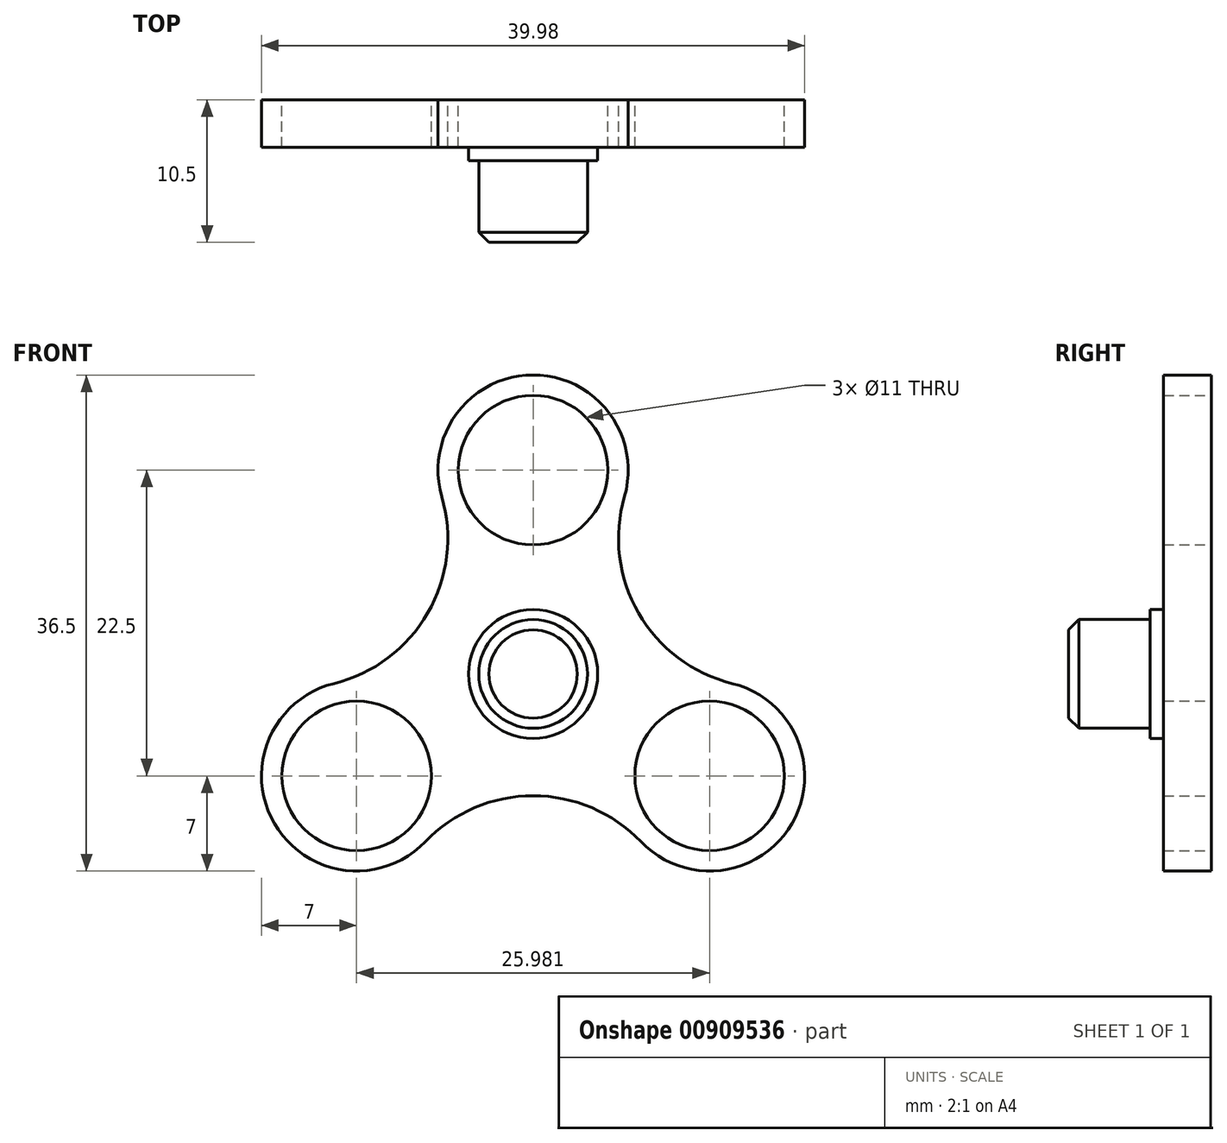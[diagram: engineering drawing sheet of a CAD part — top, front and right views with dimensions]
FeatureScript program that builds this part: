
annotation { "Feature Type Name" : "Feature", "Feature Type Description" : "" }
export const myFeature = defineFeature(function(context is Context, id is Id, definition is map)
    precondition{}
    {
        {
            var Q0;
            Q0=qCreatedBy(makeId("Front.planeOp"),FACE);
            var sketch = newSketch(context, id + "F0", { "sketchPlane" : qUnion([Q0])});
            skCircle(sketch, "E0", {"center": v(0, 0) * mm, "radius": 11 * mm});
            skCircle(sketch, "E1.cCircle", {"center": v(0, 0) * mm, "radius": 30 * mm, "construction": true});
            skLineSegment(sketch, "E1.0", {"start": v(0, 30) * mm, "end": v(25.98, -15) * mm, "construction": true});
            skLineSegment(sketch, "E1.1", {"start": v(25.98, -15) * mm, "end": v(-25.98, -15) * mm, "construction": true});
            skLineSegment(sketch, "E1.2", {"start": v(-25.98, -15) * mm, "end": v(0, 30) * mm, "construction": true});
            skArc(sketch, "E2", {"start": v(10.56, 26.93) * mm, "mid": v(0, 41) * mm, "end": v(-10.56, 26.93) * mm});
            skArc(sketch, "E3", {"start": v(-28.6, -4.32) * mm, "mid": v(-35.5, -20.5) * mm, "end": v(-18.04, -22.61) * mm});
            skArc(sketch, "E4", {"start": v(18.04, -22.61) * mm, "mid": v(35.5, -20.5) * mm, "end": v(28.6, -4.32) * mm});
            skArc(sketch, "E5", {"start": v(-28.6, -4.32) * mm, "mid": v(-12.92, 7.46) * mm, "end": v(-10.56, 26.93) * mm});
            skArc(sketch, "E6", {"start": v(18.04, -22.61) * mm, "mid": v(0, -14.92) * mm, "end": v(-18.04, -22.61) * mm});
            skArc(sketch, "E7", {"start": v(10.56, 26.93) * mm, "mid": v(12.92, 7.46) * mm, "end": v(28.6, -4.32) * mm});
            skArc(sketch, "E8.0", {"start": v(13.44, 26.1) * mm, "mid": v(15.52, 8.96) * mm, "end": v(29.32, -1.4) * mm});
            skArc(sketch, "E8.1", {"start": v(-29.32, -1.4) * mm, "mid": v(-15.52, 8.96) * mm, "end": v(-13.44, 26.1) * mm});
            skArc(sketch, "E8.2", {"start": v(-29.32, -1.4) * mm, "mid": v(-38.1, -22) * mm, "end": v(-15.88, -24.7) * mm});
            skArc(sketch, "E8.3", {"start": v(13.44, 26.1) * mm, "mid": v(0, 44) * mm, "end": v(-13.44, 26.1) * mm});
            skArc(sketch, "E8.4", {"start": v(15.88, -24.7) * mm, "mid": v(0, -17.92) * mm, "end": v(-15.88, -24.7) * mm});
            skArc(sketch, "E8.5", {"start": v(15.88, -24.7) * mm, "mid": v(38.1, -22) * mm, "end": v(29.32, -1.4) * mm});
            skCircle(sketch, "E9", {"center": v(-25.98, -15) * mm, "radius": 11 * mm});
            skCircle(sketch, "E10", {"center": v(25.98, -15) * mm, "radius": 11 * mm});
            skCircle(sketch, "E11", {"center": v(0, 30) * mm, "radius": 11 * mm});
            skSolve(sketch);
        }
        {
            var Q0;
            Q0=makeQuery(id+"F0.imprint","IMPRINT",FACE,{"disambiguationData":[TD([[makeQuery(id+"F0.imprint","IMPRINT",EDGE,{"derivedFrom":sQuery(id+"F0.wireOp",EDGE,"E0")}),-1.0]])]});
            var Q1;
            {var subQ1=sQuery(id+"F0.wireOp",EDGE,"E5");Q1=makeQuery(id+"F0.imprint","IMPRINT",FACE,{"disambiguationData":[TD([[makeQuery(id+"F0.imprint","IMPRINT",EDGE,{"derivedFrom":subQ1}),1.0]])]});}
            extrude(context, id + "F1", {"entities" : qUnion([Q0, Q1]), "depth" : 7 * mm, "offsetDistance" : 25 * mm});
        }
        {
            var Q0;
            Q0=makeQuery(id+"F1.opExtrude","SWEPT_BODY",BODY,{"disambiguationData":[OSD([sQuery(id+"F0.wireOp",EDGE,"E0"),sQuery(id+"F0.wireOp",EDGE,"E8.0"),sQuery(id+"F0.wireOp",EDGE,"E8.1"),sQuery(id+"F0.wireOp",EDGE,"E8.2"),sQuery(id+"F0.wireOp",EDGE,"E8.3"),sQuery(id+"F0.wireOp",EDGE,"E8.4"),sQuery(id+"F0.wireOp",EDGE,"E8.5"),sQuery(id+"F0.wireOp",EDGE,"E9"),sQuery(id+"F0.wireOp",EDGE,"E10"),sQuery(id+"F0.wireOp",EDGE,"E11")])]});
            var Q1;
            Q1=qCreatedBy(makeId("Origin.pointOp"),VERTEX);
            transform(context, id + "F2", {"entities" : qUnion([Q0]), "transformType" : TransformType.SCALE_UNIFORMLY, "scale" : 1 / 2, "scalePoint" : qUnion([Q1]), "makeCopy" : false});
        }
        {
            var Q0;
            Q0=qCreatedBy(makeId("Right.planeOp"),FACE);
            var sketch = newSketch(context, id + "F3", { "sketchPlane" : qUnion([Q0])});
            skLineSegment(sketch, "E12", {"start": v(-3.5, 9.5) * mm, "end": v(-3.5, 9.5) * mm});
            skLineSegment(sketch, "E13", {"start": v(-2.8, 20.5) * mm, "end": v(-2.8, 20.5) * mm});
            skLineSegment(sketch, "E14.bottom", {"start": v(-10.5, 19) * mm, "end": v(-3.5, 19) * mm});
            skLineSegment(sketch, "E14.top", {"start": v(-10.5, 15) * mm, "end": v(-3.5, 15) * mm});
            skLineSegment(sketch, "E14.left", {"start": v(-10.5, 19) * mm, "end": v(-10.5, 15) * mm});
            skLineSegment(sketch, "E14.right", {"start": v(-3.5, 19) * mm, "end": v(-3.5, 15) * mm});
            skLineSegment(sketch, "E15", {"start": v(0, 9.5) * mm, "end": v(-3.5, 9.5) * mm});
            skLineSegment(sketch, "E16", {"start": v(-3.5, 20.5) * mm, "end": v(0, 20.5) * mm});
            skLineSegment(sketch, "E17.0.0", {"start": v(-3.5, -12.35) * mm, "end": v(-3.5, -8.96) * mm});
            skLineSegment(sketch, "E17.0.1", {"start": v(-3.5, -14.5) * mm, "end": v(-3.5, -0.7) * mm});
            skLineSegment(sketch, "E17.0.5", {"start": v(-3.5, -0.7) * mm, "end": v(-3.5, -14.5) * mm});
            skLineSegment(sketch, "E18", {"start": v(0, 20.5) * mm, "end": v(0, 9.5) * mm});
            skLineSegment(sketch, "E19", {"start": v(0, 15) * mm, "end": v(-15.65, 15) * mm, "construction": true});
            skLineSegment(sketch, "E20", {"start": v(-3.5, 20.5) * mm, "end": v(-3.5, 19) * mm});
            skLineSegment(sketch, "E21", {"start": v(0, 15) * mm, "end": v(-3.5, 15) * mm});
            skLineSegment(sketch, "E22", {"start": v(0, -5.5) * mm, "end": v(-3.5, -5.5) * mm});
            skLineSegment(sketch, "E23", {"start": v(-3.5, 5.5) * mm, "end": v(0, 5.5) * mm});
            skLineSegment(sketch, "E24", {"start": v(0, -5.5) * mm, "end": v(0, 0) * mm});
            skLineSegment(sketch, "E25.bottom", {"start": v(-3.5, 0) * mm, "end": v(-10.5, 0) * mm});
            skLineSegment(sketch, "E25.top", {"start": v(-3.5, -4) * mm, "end": v(-10.5, -4) * mm});
            skLineSegment(sketch, "E25.left", {"start": v(-3.5, 0) * mm, "end": v(-3.5, -4) * mm});
            skLineSegment(sketch, "E25.right", {"start": v(-10.5, 0) * mm, "end": v(-10.5, -4) * mm});
            skLineSegment(sketch, "E26", {"start": v(-3.5, -4) * mm, "end": v(-3.5, -5.5) * mm});
            skLineSegment(sketch, "E27", {"start": v(-3.5, 0) * mm, "end": v(0, 0) * mm});
            skSolve(sketch);
        }
        {
            var Q0;
            Q0=makeQuery(id+"F3.imprint","IMPRINT",FACE,{"disambiguationData":[TD([[makeQuery(id+"F3.imprint","IMPRINT",EDGE,{"derivedFrom":sQuery(id+"F3.wireOp",EDGE,"E25.bottom")}),1.0]])]});
            var Q1;
            {var subQ2=sQuery(id+"F3.wireOp",EDGE,"E22");Q1=makeQuery(id+"F3.imprint","IMPRINT",FACE,{"disambiguationData":[TD([[makeQuery(id+"F3.imprint","IMPRINT",EDGE,{"derivedFrom":subQ2}),-1.0]])]});}
            var Q2;
            Q2=sQuery(id+"F3.wireOp",EDGE,"E25.bottom");
            revolve(context, id + "F4", {"operationType" : NewBodyOperationType.ADD, "surfaceOperationType" : NewSurfaceOperationType.NEW, "entities" : qUnion([Q0, Q1]), "axis" : qUnion([Q2]), "revolveType" : RevolveType.FULL});
        }
        {
            var Q0;
            Q0=makeQuery(id+"F4.boolean.opBoolean","MERGE",FACE,{"derivedFrom":[makeQuery(id+"F1.opExtrude","CAP_FACE",FACE,{"disambiguationData":[OSD([sQuery(id+"F0.wireOp",EDGE,"E0"),sQuery(id+"F0.wireOp",EDGE,"E8.0"),sQuery(id+"F0.wireOp",EDGE,"E8.1"),sQuery(id+"F0.wireOp",EDGE,"E8.2"),sQuery(id+"F0.wireOp",EDGE,"E8.3"),sQuery(id+"F0.wireOp",EDGE,"E8.4"),sQuery(id+"F0.wireOp",EDGE,"E8.5"),sQuery(id+"F0.wireOp",EDGE,"E9"),sQuery(id+"F0.wireOp",EDGE,"E10"),sQuery(id+"F0.wireOp",EDGE,"E11")])],"isStart":false}),makeQuery(id+"F4.opRevolve","SWEPT_FACE",FACE,{"disambiguationData":[OSD([sQuery(id+"F3.wireOp",EDGE,"E17.0.1")])]})]});
            var sketch = newSketch(context, id + "F5", { "sketchPlane" : qUnion([Q0])});
            skCircle(sketch, "E28", {"center": v(0, 0) * mm, "radius": 4.75 * mm});
            skSolve(sketch);
        }
        {
            var Q0;
            Q0=makeQuery(id+"F5.imprint","IMPRINT",FACE,{"disambiguationData":[TD([[makeQuery(id+"F5.imprint","IMPRINT",EDGE,{"derivedFrom":sQuery(id+"F5.wireOp",EDGE,"E28")}),1.0]])]});
            extrude(context, id + "F6", {"entities" : qUnion([Q0]), "operationType" : NewBodyOperationType.ADD, "depth" : 1 * mm, "offsetDistance" : 25 * mm});
        }
        {
            var Q0;
            Q0=makeQuery(id+"F4.opRevolve","SWEPT_EDGE",EDGE,{"disambiguationData":[OSD([sQuery(id+"F3.wireOp",EDGE,"E25.top"),sQuery(id+"F3.wireOp",EDGE,"E25.right")])]});
            chamfer(context, id + "F7", {"entities" : qUnion([Q0]), "width" : .75 * mm, "tangentPropagation" : true});
        }
    });
